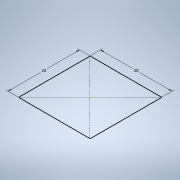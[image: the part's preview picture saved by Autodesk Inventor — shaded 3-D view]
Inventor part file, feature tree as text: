
AUTODESK INVENTOR PART (.ipt)
format: ipt  version: 2022.3 (Build 263350000, 350)  size: 136,704 bytes
history: native  units: mm
features: extrude x4, sketch x4
ambient origin geometry x8: Origin, YZ Plane, XZ Plane, XY Plane, X Axis, Y Axis, Z Axis, Center Point
bodies: Solid1 (feature_tree)
feature tree (8):
  extrude  "Extrusion1"  Depth=43.0mm
  extrude  "Extrusion3"  Depth=4.0mm
  extrude  "Extrusion4"  Depth=4.0mm
  extrude  "Extrusion5"  Depth=30.0mm TaperAngle=0.0deg
  sketch  "Sketch1"  dims[d0=44.0mm d1=43.0mm]
  sketch  "Sketch3"  dims[d2=2.0mm d3=0.0mm d7=4.0mm]
  sketch  "Sketch4"  dims[d8=9.0mm d9=4.0mm]
  sketch  "Sketch5"  dims[d10=9.0mm d11=30.0mm d12=0.0mm d13=23.0mm d14=4.0mm d15=0.0mm d16=8.0mm d17=0.0mm d18=12.0mm d19=0.0mm d20=0.0mm]
